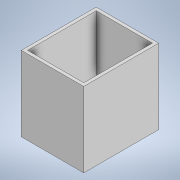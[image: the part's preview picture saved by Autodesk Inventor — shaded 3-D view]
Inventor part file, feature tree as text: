
AUTODESK INVENTOR PART (.ipt)
format: ipt  version: 2022.1 (Build 261234000, 234)  size: 96,768 bytes
history: native  units: in
note: dims shown in document units (in); Inventor stores cm internally (conversion verified against a paired STEP export)
features: extrude x1, sketch x1
ambient origin geometry x8: Origin, YZ Plane, XZ Plane, XY Plane, X Axis, Y Axis, Z Axis, Center Point
bodies: Solid1 (feature_tree)
feature tree (2):
  extrude  "Extrusion1"  Depth=2.5in
  sketch  "Sketch1"  dims[d0=3.0in d1=2.5in d2=0.125in d3=0.125in d4=3.0in d5=0.0in]
